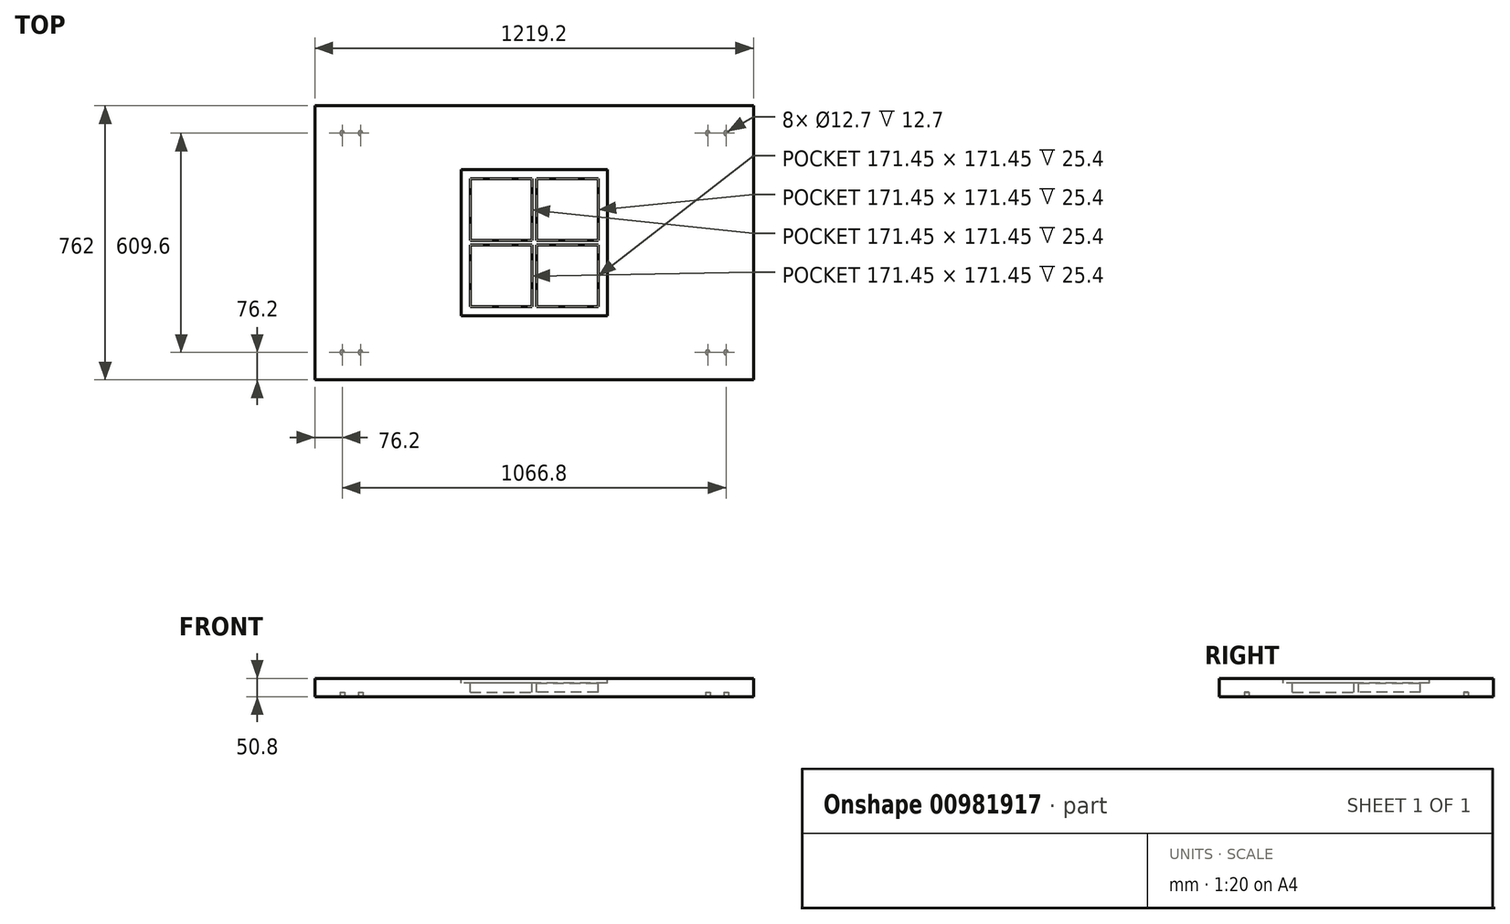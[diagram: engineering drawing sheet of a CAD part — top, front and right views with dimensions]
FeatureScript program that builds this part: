
annotation { "Feature Type Name" : "Feature", "Feature Type Description" : "" }
export const myFeature = defineFeature(function(context is Context, id is Id, definition is map)
    precondition{}
    {
        {
            var Q0;
            Q0=qCreatedBy(makeId("Top.planeOp"),FACE);
            var sketch = newSketch(context, id + "F0", { "sketchPlane" : qUnion([Q0])});
            skLineSegment(sketch, "E0", {"start": v(-609.6, 0) * mm, "end": v(609.6, 0) * mm, "construction": true});
            skLineSegment(sketch, "E1", {"start": v(0, 381) * mm, "end": v(0, -381) * mm, "construction": true});
            skLineSegment(sketch, "E2.bottom", {"start": v(-609.6, 381) * mm, "end": v(609.6, 381) * mm});
            skLineSegment(sketch, "E2.top", {"start": v(-609.6, -381) * mm, "end": v(609.6, -381) * mm});
            skLineSegment(sketch, "E2.left", {"start": v(-609.6, 381) * mm, "end": v(-609.6, -381) * mm});
            skLineSegment(sketch, "E2.right", {"start": v(609.6, 381) * mm, "end": v(609.6, -381) * mm});
            skPoint(sketch, "E3.orphan", {"position": v(-609.6, 381) * mm});
            skPoint(sketch, "E4.orphan", {"position": v(609.6, -381) * mm});
            skSolve(sketch);
        }
        {
            var Q0;
            Q0=makeQuery(id+"F0.imprint","IMPRINT",FACE,{"disambiguationData":[TD([[makeQuery(id+"F0.imprint","IMPRINT",EDGE,{"derivedFrom":sQuery(id+"F0.wireOp",EDGE,"E2.bottom")}),-1.0]])]});
            extrude(context, id + "F1", {"entities" : qUnion([Q0]), "depth" : 50.8 * mm, "offsetDistance" : 25.4 * mm});
        }
        {
            var Q0;
            Q0=makeQuery(id+"F1.opExtrude","CAP_FACE",FACE,{"disambiguationData":[OSD([sQuery(id+"F0.wireOp",EDGE,"E2.bottom"),sQuery(id+"F0.wireOp",EDGE,"E2.top"),sQuery(id+"F0.wireOp",EDGE,"E2.left"),sQuery(id+"F0.wireOp",EDGE,"E2.right"),sQuery(id+"F0.wireOp",EDGE,"XeqdrrCw-HFEN-wusJ-wyex-TqBvOqBGrOIz"),sQuery(id+"F0.wireOp",EDGE,"8fb6fc53-10cc-4bae-8172-f28ac65889710.MirrorCS"),sQuery(id+"F0.wireOp",EDGE,"58cdf947-fc7c-416b-8956-66b84beab21d0.MirrorCS"),sQuery(id+"F0.wireOp",EDGE,"16355b7c-684d-45f1-abcd-a90a74fff03e0.MirrorCS")])],"isStart":true});
            var sketch = newSketch(context, id + "F2", { "sketchPlane" : qUnion([Q0])});
            skLineSegment(sketch, "E5", {"start": v(0, 381) * mm, "end": v(0, -381) * mm, "construction": true});
            skLineSegment(sketch, "E6", {"start": v(-609.6, 0) * mm, "end": v(609.6, 0) * mm, "construction": true});
            skCircle(sketch, "E7", {"center": v(-533.4, 304.8) * mm, "radius": 6.35 * mm});
            skCircle(sketch, "E8", {"center": v(533.4, 304.8) * mm, "radius": 6.35 * mm});
            skCircle(sketch, "E9", {"center": v(533.4, -304.8) * mm, "radius": 6.35 * mm});
            skCircle(sketch, "E10", {"center": v(-533.4, -304.8) * mm, "radius": 6.35 * mm});
            skCircle(sketch, "E11", {"center": v(-482.6, 304.8) * mm, "radius": 6.35 * mm});
            skCircle(sketch, "E12", {"center": v(482.6, 304.8) * mm, "radius": 6.35 * mm});
            skCircle(sketch, "E13", {"center": v(482.6, -304.8) * mm, "radius": 6.35 * mm});
            skCircle(sketch, "E14", {"center": v(-482.6, -304.8) * mm, "radius": 6.35 * mm});
            skLineSegment(sketch, "E15", {"start": v(-533.4, 304.8) * mm, "end": v(533.4, 304.8) * mm, "construction": true});
            skLineSegment(sketch, "E16", {"start": v(533.4, 304.8) * mm, "end": v(533.4, -304.8) * mm, "construction": true});
            skLineSegment(sketch, "E17", {"start": v(533.4, -304.8) * mm, "end": v(-533.4, -304.8) * mm, "construction": true});
            skLineSegment(sketch, "E18", {"start": v(-533.4, -304.8) * mm, "end": v(-533.4, 304.8) * mm, "construction": true});
            skLineSegment(sketch, "E19", {"start": v(-482.6, 304.8) * mm, "end": v(-482.6, -304.8) * mm, "construction": true});
            skLineSegment(sketch, "E20", {"start": v(482.6, 304.8) * mm, "end": v(482.6, -304.8) * mm, "construction": true});
            skSolve(sketch);
        }
        {
            var Q0;
            Q0 = qSketchRegion(id + "F2", true);
            extrude(context, id + "F3", {"entities" : qUnion([Q0]), "operationType" : NewBodyOperationType.REMOVE, "flatOperationType" : FlatOperationType.REMOVE, "oppositeDirection" : true, "depth" : 12.7 * mm, "offsetDistance" : 25.4 * mm, "domain" : OperationDomain.MODEL});
        }
        {
            var Q0;
            Q0=makeQuery(id+"F1.opExtrude","CAP_FACE",FACE,{"disambiguationData":[OSD([sQuery(id+"F0.wireOp",EDGE,"E2.bottom"),sQuery(id+"F0.wireOp",EDGE,"E2.top"),sQuery(id+"F0.wireOp",EDGE,"E2.left"),sQuery(id+"F0.wireOp",EDGE,"E2.right"),sQuery(id+"F0.wireOp",EDGE,"XeqdrrCw-HFEN-wusJ-wyex-TqBvOqBGrOIz"),sQuery(id+"F0.wireOp",EDGE,"8fb6fc53-10cc-4bae-8172-f28ac65889710.MirrorCS"),sQuery(id+"F0.wireOp",EDGE,"58cdf947-fc7c-416b-8956-66b84beab21d0.MirrorCS"),sQuery(id+"F0.wireOp",EDGE,"16355b7c-684d-45f1-abcd-a90a74fff03e0.MirrorCS")])],"isStart":false});
            var sketch = newSketch(context, id + "F4", { "sketchPlane" : qUnion([Q0])});
            skLineSegment(sketch, "E21", {"start": v(0, 381) * mm, "end": v(0, -381) * mm, "construction": true});
            skLineSegment(sketch, "E22", {"start": v(-609.6, 0) * mm, "end": v(609.6, 0) * mm, "construction": true});
            skLineSegment(sketch, "E23.bottom", {"start": v(-177.8, 177.8) * mm, "end": v(-6.35, 177.8) * mm});
            skLineSegment(sketch, "E23.top", {"start": v(-177.8, 6.35) * mm, "end": v(-6.35, 6.35) * mm});
            skLineSegment(sketch, "E23.left", {"start": v(-177.8, 177.8) * mm, "end": v(-177.8, 6.35) * mm});
            skLineSegment(sketch, "E23.right", {"start": v(-6.35, 177.8) * mm, "end": v(-6.35, 6.35) * mm});
            skLineSegment(sketch, "E24.bottom", {"start": v(177.8, 177.8) * mm, "end": v(6.35, 177.8) * mm});
            skLineSegment(sketch, "E24.top", {"start": v(177.8, 6.35) * mm, "end": v(6.35, 6.35) * mm});
            skLineSegment(sketch, "E24.left", {"start": v(177.8, 177.8) * mm, "end": v(177.8, 6.35) * mm});
            skLineSegment(sketch, "E24.right", {"start": v(6.35, 177.8) * mm, "end": v(6.35, 6.35) * mm});
            skLineSegment(sketch, "E25.bottom", {"start": v(177.8, -177.8) * mm, "end": v(6.35, -177.8) * mm});
            skLineSegment(sketch, "E25.top", {"start": v(177.8, -6.35) * mm, "end": v(6.35, -6.35) * mm});
            skLineSegment(sketch, "E25.left", {"start": v(177.8, -177.8) * mm, "end": v(177.8, -6.35) * mm});
            skLineSegment(sketch, "E25.right", {"start": v(6.35, -177.8) * mm, "end": v(6.35, -6.35) * mm});
            skLineSegment(sketch, "E26.bottom", {"start": v(-177.8, -177.8) * mm, "end": v(-6.35, -177.8) * mm});
            skLineSegment(sketch, "E26.top", {"start": v(-177.8, -6.35) * mm, "end": v(-6.35, -6.35) * mm});
            skLineSegment(sketch, "E26.left", {"start": v(-177.8, -177.8) * mm, "end": v(-177.8, -6.35) * mm});
            skLineSegment(sketch, "E26.right", {"start": v(-6.35, -177.8) * mm, "end": v(-6.35, -6.35) * mm});
            skSolve(sketch);
        }
        {
            var Q0;
            Q0 = qSketchRegion(id + "F4", true);
            extrude(context, id + "F5", {"entities" : qUnion([Q0]), "operationType" : NewBodyOperationType.REMOVE, "flatOperationType" : FlatOperationType.REMOVE, "oppositeDirection" : true, "depth" : 38.1 * mm, "offsetDistance" : 25.4 * mm, "domain" : OperationDomain.MODEL});
        }
        {
            var Q0;
            Q0=makeQuery(id+"F1.opExtrude","CAP_FACE",FACE,{"disambiguationData":[OSD([sQuery(id+"F0.wireOp",EDGE,"E2.bottom"),sQuery(id+"F0.wireOp",EDGE,"E2.top"),sQuery(id+"F0.wireOp",EDGE,"E2.left"),sQuery(id+"F0.wireOp",EDGE,"E2.right"),sQuery(id+"F0.wireOp",EDGE,"XeqdrrCw-HFEN-wusJ-wyex-TqBvOqBGrOIz"),sQuery(id+"F0.wireOp",EDGE,"8fb6fc53-10cc-4bae-8172-f28ac65889710.MirrorCS"),sQuery(id+"F0.wireOp",EDGE,"58cdf947-fc7c-416b-8956-66b84beab21d0.MirrorCS"),sQuery(id+"F0.wireOp",EDGE,"16355b7c-684d-45f1-abcd-a90a74fff03e0.MirrorCS")])],"isStart":false});
            var sketch = newSketch(context, id + "F6", { "sketchPlane" : qUnion([Q0])});
            skLineSegment(sketch, "E27.bottom", {"start": v(203.2, 203.2) * mm, "end": v(-203.2, 203.2) * mm});
            skLineSegment(sketch, "E27.top", {"start": v(203.2, -203.2) * mm, "end": v(-203.2, -203.2) * mm});
            skLineSegment(sketch, "E27.left", {"start": v(203.2, 203.2) * mm, "end": v(203.2, -203.2) * mm});
            skLineSegment(sketch, "E27.right", {"start": v(-203.2, 203.2) * mm, "end": v(-203.2, -203.2) * mm});
            skPoint(sketch, "E27.middle", {"position": v(0, 0) * mm});
            skSolve(sketch);
        }
        {
            var Q0;
            Q0 = qSketchRegion(id + "F6", true);
            extrude(context, id + "F7", {"entities" : qUnion([Q0]), "operationType" : NewBodyOperationType.REMOVE, "flatOperationType" : FlatOperationType.REMOVE, "oppositeDirection" : true, "depth" : 12.7 * mm, "offsetDistance" : 25.4 * mm, "domain" : OperationDomain.MODEL});
        }
    });
